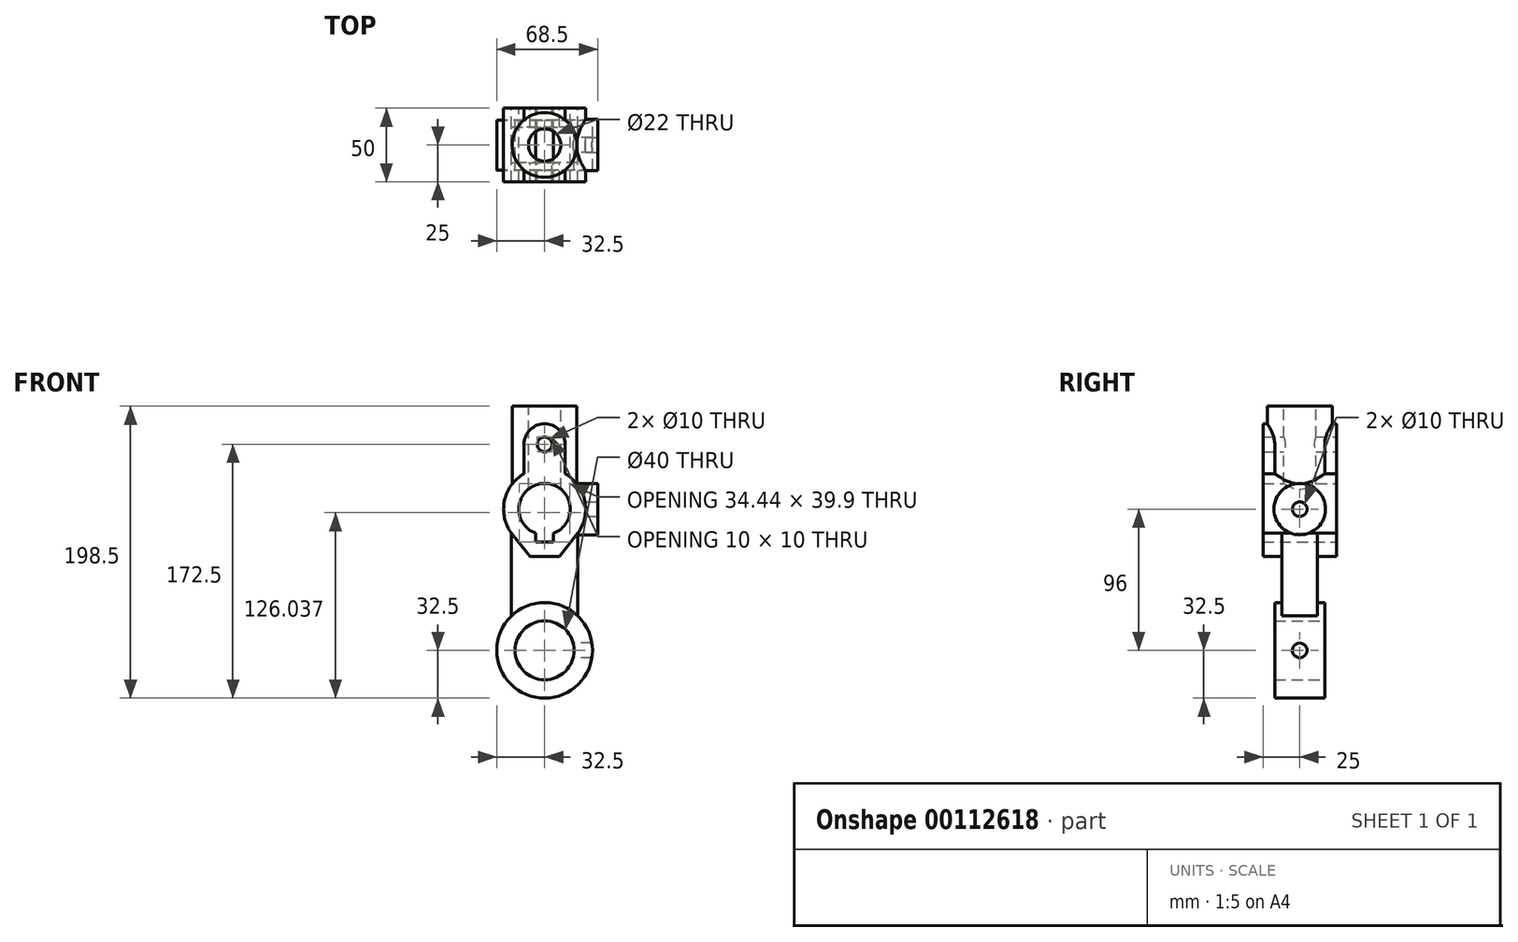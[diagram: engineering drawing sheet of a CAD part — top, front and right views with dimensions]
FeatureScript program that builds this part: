
annotation { "Feature Type Name" : "Feature", "Feature Type Description" : "" }
export const myFeature = defineFeature(function(context is Context, id is Id, definition is map)
    precondition{}
    {
        {
            var Q0;
            Q0=qCreatedBy(makeId("Front.planeOp"),FACE);
            var sketch = newSketch(context, id + "F0", { "sketchPlane" : qUnion([Q0])});
            skCircle(sketch, "E0", {"center": v(0, 0) * mm, "radius": 20 * mm});
            skCircle(sketch, "E1", {"center": v(0, 0) * mm, "radius": 32.5 * mm});
            skLineSegment(sketch, "E2", {"start": v(0, 0) * mm, "end": v(0, 268.23) * mm, "construction": true});
            skArc(sketch, "E3", {"start": v(6, 79.57) * mm, "mid": v(0, 113.49) * mm, "end": v(-6, 79.57) * mm});
            skLineSegment(sketch, "E4", {"start": v(-6, 79.57) * mm, "end": v(-6, 73.59) * mm});
            skLineSegment(sketch, "E5", {"start": v(6, 79.57) * mm, "end": v(6, 73.59) * mm});
            skLineSegment(sketch, "E6", {"start": v(6, 73.59) * mm, "end": v(-6, 73.59) * mm});
            skCircle(sketch, "E7", {"center": v(0, 140) * mm, "radius": 5 * mm});
            skLineSegment(sketch, "E8", {"start": v(-22.5, 166) * mm, "end": v(-22.5, 23.45) * mm});
            skLineSegment(sketch, "E9", {"start": v(22.5, 23.45) * mm, "end": v(22.5, 166) * mm});
            skLineSegment(sketch, "E10", {"start": v(-22.5, 166) * mm, "end": v(22.5, 166) * mm});
            skLineSegment(sketch, "E11", {"start": v(-14, 140) * mm, "end": v(-14, 120.08) * mm});
            skLineSegment(sketch, "E12", {"start": v(14, 140) * mm, "end": v(14, 120.08) * mm});
            skArc(sketch, "E13", {"start": v(-14, 140) * mm, "mid": v(0, 154) * mm, "end": v(14, 140) * mm});
            skLineSegment(sketch, "E14", {"start": v(-22.5, 79.57) * mm, "end": v(-10, 63.96) * mm});
            skLineSegment(sketch, "E15", {"start": v(22.5, 79.57) * mm, "end": v(10, 63.96) * mm});
            skLineSegment(sketch, "E16", {"start": v(-10, 63.96) * mm, "end": v(10, 63.96) * mm});
            skArc(sketch, "E17", {"start": v(-14, 120.08) * mm, "mid": v(-27.26, 101.72) * mm, "end": v(-22.5, 79.57) * mm});
            skArc(sketch, "E18", {"start": v(22.5, 79.57) * mm, "mid": v(27.26, 101.72) * mm, "end": v(14, 120.08) * mm});
            skSolve(sketch);
        }
        {
            var Q0;
            Q0=makeQuery(id+"F0.imprint","IMPRINT",FACE,{"disambiguationData":[TD([[makeQuery(id+"F0.imprint","IMPRINT",EDGE,{"derivedFrom":sQuery(id+"F0.wireOp",EDGE,"E3")}),-1.0]])]});
            var Q1;
            {var subQ0=sQuery(id+"F0.wireOp",EDGE,"E18");var subQ1=sQuery(id+"F0.wireOp",EDGE,"E9");var subQ3=makeQuery(id+"F0.imprint","INTERSECT",VERTEX,{"derivedFrom":[subQ1,subQ0]});Q1=makeQuery(id+"F0.imprint","IMPRINT",FACE,{"disambiguationData":[TD([[makeQuery(id+"F0.imprint","IMPRINT",EDGE,{"disambiguationData":[TD([[subQ3,1.0]])],"derivedFrom":subQ1}),-1.0]])]});}
            var Q2;
            {var subQ0=sQuery(id+"F0.wireOp",EDGE,"E17");var subQ1=sQuery(id+"F0.wireOp",EDGE,"E8");var subQ3=makeQuery(id+"F0.imprint","INTERSECT",VERTEX,{"derivedFrom":[subQ1,subQ0]});Q2=makeQuery(id+"F0.imprint","IMPRINT",FACE,{"disambiguationData":[TD([[makeQuery(id+"F0.imprint","IMPRINT",EDGE,{"disambiguationData":[TD([[subQ3,-1.0]])],"derivedFrom":subQ1}),-1.0]])]});}
            extrude(context, id + "F1", {"entities" : qUnion([Q0, Q1, Q2]), "endBound" : BoundingType.SYMMETRIC, "depth" : 50 * mm});
        }
        {
            var Q0;
            {var subQ6=sQuery(id+"F0.wireOp",EDGE,"E14");Q0=makeQuery(id+"F0.imprint","IMPRINT",FACE,{"disambiguationData":[TD([[makeQuery(id+"F0.imprint","IMPRINT",EDGE,{"derivedFrom":subQ6}),-1.0]])]});}
            extrude(context, id + "F2", {"entities" : qUnion([Q0]), "operationType" : NewBodyOperationType.ADD, "endBound" : BoundingType.SYMMETRIC, "depth" : 24 * mm});
        }
        {
            var Q0;
            Q0=makeQuery(id+"F0.imprint","IMPRINT",FACE,{"disambiguationData":[TD([[makeQuery(id+"F0.imprint","IMPRINT",EDGE,{"derivedFrom":sQuery(id+"F0.wireOp",EDGE,"E0")}),-1.0]])]});
            extrude(context, id + "F3", {"entities" : qUnion([Q0]), "operationType" : NewBodyOperationType.ADD, "endBound" : BoundingType.SYMMETRIC, "depth" : 34 * mm});
        }
        {
            var Q0;
            Q0=sQuery(id+"F0.wireOp",EDGE,"E10");
            cPlane(context, id + "F4", {"entities" : qUnion([Q0]), "cplaneType" : CPlaneType.LINE_ANGLE, "offset" : 25 * mm, "angle" : 90 * degree, "width" : 150 * mm, "height" : 150 * mm});
        }
        {
            var Q0;
            Q0=qCreatedBy(id+"F4.planeOp",FACE);
            var sketch = newSketch(context, id + "F5", { "sketchPlane" : qUnion([Q0])});
            skCircle(sketch, "E19", {"center": v(0, 0) * mm, "radius": 11 * mm});
            skCircle(sketch, "E20", {"center": v(0, 0) * mm, "radius": 22 * mm});
            skSolve(sketch);
        }
        {
            var Q0;
            Q0=makeQuery(id+"F5.imprint","IMPRINT",FACE,{"disambiguationData":[TD([[makeQuery(id+"F5.imprint","IMPRINT",EDGE,{"derivedFrom":sQuery(id+"F5.wireOp",EDGE,"E19")}),-1.0]])]});
            extrude(context, id + "F6", {"entities" : qUnion([Q0]), "operationType" : NewBodyOperationType.ADD, "endBound" : BoundingType.UP_TO_NEXT, "oppositeDirection" : true, "depth" : 25 * mm});
        }
        {
            var Q0;
            Q0=makeQuery(id+"F5.imprint","IMPRINT",FACE,{"disambiguationData":[TD([[makeQuery(id+"F5.imprint","IMPRINT",EDGE,{"derivedFrom":sQuery(id+"F5.wireOp",EDGE,"E19")}),1.0]])]});
            extrude(context, id + "F7", {"entities" : qUnion([Q0]), "operationType" : NewBodyOperationType.REMOVE, "oppositeDirection" : true, "depth" : 70 * mm});
        }
        {
            var Q0;
            Q0=qCreatedBy(makeId("Right.planeOp"),FACE);
            var sketch = newSketch(context, id + "F8", { "sketchPlane" : qUnion([Q0])});
            skCircle(sketch, "E21", {"center": v(0, 0) * mm, "radius": 5 * mm});
            skSolve(sketch);
        }
        {
            var Q0;
            Q0=makeQuery(id+"F8.imprint","IMPRINT",FACE,{"disambiguationData":[TD([[makeQuery(id+"F8.imprint","IMPRINT",EDGE,{"derivedFrom":sQuery(id+"F8.wireOp",EDGE,"E21")}),1.0]])]});
            extrude(context, id + "F9", {"entities" : qUnion([Q0]), "operationType" : NewBodyOperationType.REMOVE, "depth" : 65 * mm});
        }
        {
            var Q0;
            Q0=qCreatedBy(makeId("Right.planeOp"),FACE);
            cPlane(context, id + "F10", {"entities" : qUnion([Q0]), "cplaneType" : CPlaneType.OFFSET, "offset" : 36 * mm, "width" : 150 * mm, "height" : 150 * mm});
        }
        {
            var Q0;
            Q0=qCreatedBy(id+"F10.planeOp",FACE);
            var sketch = newSketch(context, id + "F11", { "sketchPlane" : qUnion([Q0])});
            skPoint(sketch, "E22.0", {"position": v(0, 96) * mm});
            skCircle(sketch, "E23", {"center": v(0, 96) * mm, "radius": 5 * mm});
            skCircle(sketch, "E24", {"center": v(0, 96) * mm, "radius": 17.5 * mm});
            skSolve(sketch);
        }
        {
            var Q0;
            Q0=makeQuery(id+"F11.imprint","IMPRINT",FACE,{"disambiguationData":[TD([[makeQuery(id+"F11.imprint","IMPRINT",EDGE,{"derivedFrom":sQuery(id+"F11.wireOp",EDGE,"E23")}),-1.0]])]});
            var Q1;
            Q1=makeQuery(id+"F1.opExtrude","SWEPT_FACE",FACE,{"disambiguationData":[OSD([sQuery(id+"F0.wireOp",EDGE,"E18")])]});
            extrude(context, id + "F12", {"entities" : qUnion([Q0]), "operationType" : NewBodyOperationType.ADD, "endBound" : BoundingType.UP_TO_SURFACE, "oppositeDirection" : true, "endBoundEntityFace" : qUnion([Q1]), "depth" : 25 * mm});
        }
    });
